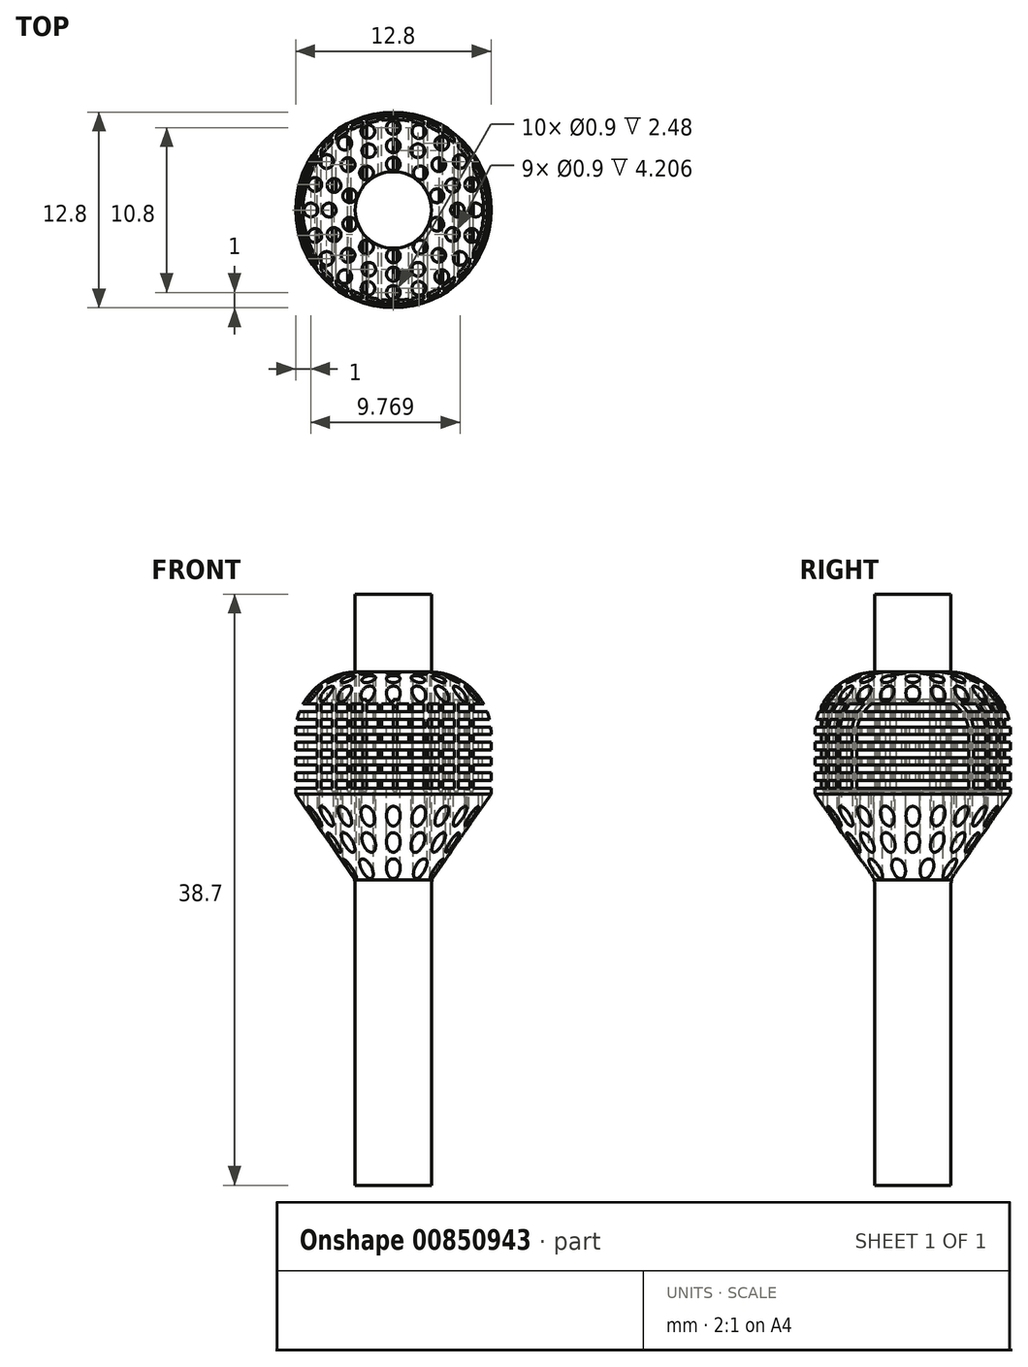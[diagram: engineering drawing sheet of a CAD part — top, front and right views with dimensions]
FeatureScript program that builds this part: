
annotation { "Feature Type Name" : "Feature", "Feature Type Description" : "" }
export const myFeature = defineFeature(function(context is Context, id is Id, definition is map)
    precondition{}
    {
        {
            var Q0;
            Q0=qCreatedBy(makeId("Front.planeOp"),FACE);
            var sketch = newSketch(context, id + "F0", { "sketchPlane" : qUnion([Q0])});
            skLineSegment(sketch, "E0", {"start": v(0, 0) * mm, "end": v(0, -20) * mm});
            skLineSegment(sketch, "E1", {"start": v(0, -20) * mm, "end": v(2.5, -20) * mm});
            skLineSegment(sketch, "E2", {"start": v(2.5, -20) * mm, "end": v(2.5, -0.32) * mm});
            skLineSegment(sketch, "E3", {"start": v(2.68, 0.26) * mm, "end": v(6.33, 5.48) * mm});
            skLineSegment(sketch, "E4", {"start": v(6.52, 6.05) * mm, "end": v(6.52, 9.73) * mm});
            skArc(sketch, "E5", {"start": v(6.52, 9.73) * mm, "mid": v(5.34, 12.57) * mm, "end": v(2.5, 13.73) * mm});
            skLineSegment(sketch, "E6", {"start": v(2.5, 13.73) * mm, "end": v(0, 13.72) * mm});
            skLineSegment(sketch, "E7", {"start": v(0, 0) * mm, "end": v(0, 13.72) * mm});
            skPoint(sketch, "E8.visualSharp", {"position": v(2.5, 0) * mm});
            skArc(sketch, "E8.filletArc", {"start": v(2.68, 0.26) * mm, "mid": v(2.55, -0.01) * mm, "end": v(2.5, -0.32) * mm});
            skPoint(sketch, "E9.visualSharp", {"position": v(6.52, 5.73) * mm});
            skArc(sketch, "E9.filletArc", {"start": v(6.33, 5.48) * mm, "mid": v(6.47, 5.75) * mm, "end": v(6.52, 6.05) * mm});
            skSolve(sketch);
        }
        {
            var Q0;
            Q0=makeQuery(id+"F0.imprint","IMPRINT",FACE,{"disambiguationData":[TD([[makeQuery(id+"F0.imprint","IMPRINT",EDGE,{"derivedFrom":sQuery(id+"F0.wireOp",EDGE,"E0")}),1.0]])]});
            var Q1;
            Q1=sQuery(id+"F0.wireOp",EDGE,"E7");
            revolve(context, id + "F1", {"surfaceOperationType" : NewSurfaceOperationType.NEW, "entities" : qUnion([Q0]), "axis" : qUnion([Q1]), "revolveType" : RevolveType.FULL});
        }
        {
            var Q0;
            Q0=qCreatedBy(makeId("Front.planeOp"),FACE);
            var sketch = newSketch(context, id + "F2", { "sketchPlane" : qUnion([Q0])});
            skLineSegment(sketch, "E10.bottom", {"start": v(2.5, 11.5) * mm, "end": v(7.5, 11.5) * mm});
            skLineSegment(sketch, "E10.top", {"start": v(2.5, 11) * mm, "end": v(7.5, 11) * mm});
            skLineSegment(sketch, "E10.left", {"start": v(2.5, 11.5) * mm, "end": v(2.5, 11) * mm});
            skLineSegment(sketch, "E10.right", {"start": v(7.5, 11.5) * mm, "end": v(7.5, 11) * mm});
            skLineSegment(sketch, "E11.0.1.0", {"start": v(2.5, 10) * mm, "end": v(7.5, 10) * mm});
            skLineSegment(sketch, "E11.0.1.1", {"start": v(2.5, 10.5) * mm, "end": v(7.5, 10.5) * mm});
            skLineSegment(sketch, "E11.0.1.2", {"start": v(2.5, 10.5) * mm, "end": v(2.5, 10) * mm});
            skLineSegment(sketch, "E11.0.1.3", {"start": v(7.5, 10.5) * mm, "end": v(7.5, 10) * mm});
            skLineSegment(sketch, "E11.0.2.0", {"start": v(2.5, 9) * mm, "end": v(7.5, 9) * mm});
            skLineSegment(sketch, "E11.0.2.1", {"start": v(2.5, 9.5) * mm, "end": v(7.5, 9.5) * mm});
            skLineSegment(sketch, "E11.0.2.2", {"start": v(2.5, 9.5) * mm, "end": v(2.5, 9) * mm});
            skLineSegment(sketch, "E11.0.2.3", {"start": v(7.5, 9.5) * mm, "end": v(7.5, 9) * mm});
            skLineSegment(sketch, "E11.0.3.0", {"start": v(2.5, 8) * mm, "end": v(7.5, 8) * mm});
            skLineSegment(sketch, "E11.0.3.1", {"start": v(2.5, 8.5) * mm, "end": v(7.5, 8.5) * mm});
            skLineSegment(sketch, "E11.0.3.2", {"start": v(2.5, 8.5) * mm, "end": v(2.5, 8) * mm});
            skLineSegment(sketch, "E11.0.3.3", {"start": v(7.5, 8.5) * mm, "end": v(7.5, 8) * mm});
            skLineSegment(sketch, "E11.direction1", {"start": v(2.5, 11) * mm, "end": v(27.5, 11) * mm, "construction": true});
            skLineSegment(sketch, "E11.direction2", {"start": v(2.5, 11) * mm, "end": v(2.5, 10) * mm, "construction": true});
            skLineSegment(sketch, "E12.0.0.4", {"start": v(2.5, 7) * mm, "end": v(7.5, 7) * mm});
            skLineSegment(sketch, "E12.3.0.4", {"start": v(2.5, 7.5) * mm, "end": v(7.5, 7.5) * mm});
            skLineSegment(sketch, "E12.6.0.4", {"start": v(2.5, 7.5) * mm, "end": v(2.5, 7) * mm});
            skLineSegment(sketch, "E12.9.0.4", {"start": v(7.5, 7.5) * mm, "end": v(7.5, 7) * mm});
            skLineSegment(sketch, "E13.0.0.5", {"start": v(2.5, 6) * mm, "end": v(7.5, 6) * mm});
            skLineSegment(sketch, "E13.3.0.5", {"start": v(2.5, 6.5) * mm, "end": v(7.5, 6.5) * mm});
            skLineSegment(sketch, "E13.6.0.5", {"start": v(2.5, 6.5) * mm, "end": v(2.5, 6) * mm});
            skLineSegment(sketch, "E13.9.0.5", {"start": v(7.5, 6.5) * mm, "end": v(7.5, 6) * mm});
            skSolve(sketch);
        }
        {
            var Q0;
            Q0=qCreatedBy(makeId("Front.planeOp"),FACE);
            var sketch = newSketch(context, id + "F3", { "sketchPlane" : qUnion([Q0])});
            skLineSegment(sketch, "E14", {"start": v(0, 35.11) * mm, "end": v(0, -39.83) * mm, "construction": true});
            skSolve(sketch);
        }
        {
            var Q0;
            Q0 = qSketchRegion(id + "F2", true);
            var Q1;
            Q1=sQuery(id+"F3.wireOp",EDGE,"E14");
            var Q2;
            Q2 = qConstructionFilter(qBodyType(qCreatedBy(id + "F2" ,EDGE), BodyType.WIRE), ConstructionObject.NO);
            var Q3;
            Q3=sQuery(id+"F3.wireOp",EDGE,"E14");
            revolve(context, id + "F4", {"operationType" : NewBodyOperationType.REMOVE, "surfaceOperationType" : NewSurfaceOperationType.NEW, "entities" : qUnion([Q0]), "surfaceEntities" : qUnion([Q1, Q2]), "axis" : qUnion([Q3]), "revolveType" : RevolveType.FULL, "oppositeDirection" : true});
        }
        {
            var Q0;
            Q0=qCreatedBy(makeId("Top.planeOp"),FACE);
            cPlane(context, id + "F5", {"entities" : qUnion([Q0]), "cplaneType" : CPlaneType.OFFSET, "offset" : 13.7 * mm, "width" : 150 * mm, "height" : 150 * mm});
        }
        {
            var Q0;
            Q0=qCreatedBy(id+"F5.planeOp",FACE);
            var sketch = newSketch(context, id + "F6", { "sketchPlane" : qUnion([Q0])});
            skCircle(sketch, "E15", {"center": v(0, 3) * mm, "radius": 0.45 * mm});
            skCircle(sketch, "E16.1.0", {"center": v(-1.76, 2.43) * mm, "radius": 0.45 * mm});
            skCircle(sketch, "E16.2.0", {"center": v(-2.85, 0.93) * mm, "radius": 0.45 * mm});
            skCircle(sketch, "E16.3.0", {"center": v(-2.85, -0.93) * mm, "radius": 0.45 * mm});
            skCircle(sketch, "E16.4.0", {"center": v(-1.76, -2.43) * mm, "radius": 0.45 * mm});
            skCircle(sketch, "E16.5.0", {"center": v(0, -3) * mm, "radius": 0.45 * mm});
            skCircle(sketch, "E16.6.0", {"center": v(1.76, -2.43) * mm, "radius": 0.45 * mm});
            skCircle(sketch, "E16.7.0", {"center": v(2.85, -0.93) * mm, "radius": 0.45 * mm});
            skCircle(sketch, "E16.8.0", {"center": v(2.85, 0.93) * mm, "radius": 0.45 * mm});
            skCircle(sketch, "E16.9.0", {"center": v(1.76, 2.43) * mm, "radius": 0.45 * mm});
            skPoint(sketch, "E16.center", {"position": v(0, 0) * mm});
            skCircle(sketch, "E17", {"center": v(0, 4.2) * mm, "radius": 0.45 * mm});
            skCircle(sketch, "E18.1.0", {"center": v(-1.6, 3.88) * mm, "radius": 0.45 * mm});
            skCircle(sketch, "E18.2.0", {"center": v(-2.97, 2.97) * mm, "radius": 0.45 * mm});
            skCircle(sketch, "E18.3.0", {"center": v(-3.88, 1.6) * mm, "radius": 0.45 * mm});
            skCircle(sketch, "E18.4.0", {"center": v(-4.2, 0) * mm, "radius": 0.45 * mm});
            skCircle(sketch, "E18.5.0", {"center": v(-3.88, -1.6) * mm, "radius": 0.45 * mm});
            skCircle(sketch, "E18.6.0", {"center": v(-2.97, -2.97) * mm, "radius": 0.45 * mm});
            skCircle(sketch, "E18.7.0", {"center": v(-1.6, -3.88) * mm, "radius": 0.45 * mm});
            skCircle(sketch, "E18.8.0", {"center": v(0, -4.2) * mm, "radius": 0.45 * mm});
            skCircle(sketch, "E18.9.0", {"center": v(1.6, -3.88) * mm, "radius": 0.45 * mm});
            skCircle(sketch, "E18.10.0", {"center": v(2.97, -2.97) * mm, "radius": 0.45 * mm});
            skCircle(sketch, "E18.11.0", {"center": v(3.88, -1.6) * mm, "radius": 0.45 * mm});
            skCircle(sketch, "E18.12.0", {"center": v(4.2, 0) * mm, "radius": 0.45 * mm});
            skCircle(sketch, "E18.13.0", {"center": v(3.88, 1.6) * mm, "radius": 0.45 * mm});
            skCircle(sketch, "E18.14.0", {"center": v(2.97, 2.97) * mm, "radius": 0.45 * mm});
            skCircle(sketch, "E18.15.0", {"center": v(1.6, 3.88) * mm, "radius": 0.45 * mm});
            skCircle(sketch, "E19", {"center": v(0, 5.4) * mm, "radius": 0.45 * mm});
            skCircle(sketch, "E20.1.0", {"center": v(-1.67, 5.14) * mm, "radius": 0.45 * mm});
            skCircle(sketch, "E20.2.0", {"center": v(-3.17, 4.37) * mm, "radius": 0.45 * mm});
            skCircle(sketch, "E20.3.0", {"center": v(-4.37, 3.17) * mm, "radius": 0.45 * mm});
            skCircle(sketch, "E20.4.0", {"center": v(-5.14, 1.67) * mm, "radius": 0.45 * mm});
            skCircle(sketch, "E20.5.0", {"center": v(-5.4, 0) * mm, "radius": 0.45 * mm});
            skCircle(sketch, "E20.6.0", {"center": v(-5.14, -1.67) * mm, "radius": 0.45 * mm});
            skCircle(sketch, "E20.7.0", {"center": v(-4.37, -3.17) * mm, "radius": 0.45 * mm});
            skCircle(sketch, "E20.8.0", {"center": v(-3.17, -4.37) * mm, "radius": 0.45 * mm});
            skCircle(sketch, "E20.9.0", {"center": v(-1.67, -5.14) * mm, "radius": 0.45 * mm});
            skCircle(sketch, "E20.10.0", {"center": v(0, -5.4) * mm, "radius": 0.45 * mm});
            skCircle(sketch, "E20.11.0", {"center": v(1.67, -5.14) * mm, "radius": 0.45 * mm});
            skCircle(sketch, "E20.12.0", {"center": v(3.17, -4.37) * mm, "radius": 0.45 * mm});
            skCircle(sketch, "E20.13.0", {"center": v(4.37, -3.17) * mm, "radius": 0.45 * mm});
            skCircle(sketch, "E20.14.0", {"center": v(5.14, -1.67) * mm, "radius": 0.45 * mm});
            skCircle(sketch, "E20.15.0", {"center": v(5.4, 0) * mm, "radius": 0.45 * mm});
            skCircle(sketch, "E20.16.0", {"center": v(5.14, 1.67) * mm, "radius": 0.45 * mm});
            skCircle(sketch, "E20.17.0", {"center": v(4.37, 3.17) * mm, "radius": 0.45 * mm});
            skCircle(sketch, "E20.18.0", {"center": v(3.17, 4.37) * mm, "radius": 0.45 * mm});
            skCircle(sketch, "E20.19.0", {"center": v(1.67, 5.14) * mm, "radius": 0.45 * mm});
            skSolve(sketch);
        }
        {
            var Q0;
            Q0 = qSketchRegion(id + "F6", true);
            extrude(context, id + "F7", {"entities" : qUnion([Q0]), "operationType" : NewBodyOperationType.REMOVE, "oppositeDirection" : true, "depth" : 16.5 * mm, "offsetDistance" : 25 * mm});
        }
        {
            var Q0;
            Q0=qCreatedBy(makeId("Front.planeOp"),FACE);
            cPlane(context, id + "F8", {"entities" : qUnion([Q0]), "cplaneType" : CPlaneType.OFFSET, "offset" : 6 * mm, "width" : 150 * mm, "height" : 150 * mm});
        }
        {
            var Q0;
            Q0=qCreatedBy(id+"F8.planeOp",FACE);
            var sketch = newSketch(context, id + "F9", { "sketchPlane" : qUnion([Q0])});
            skLineSegment(sketch, "E21.bottom", {"start": v(-4.75, 11.8) * mm, "end": v(-5, 11.8) * mm});
            skLineSegment(sketch, "E21.top", {"start": v(-4.75, 5.8) * mm, "end": v(-5, 5.8) * mm});
            skLineSegment(sketch, "E21.left", {"start": v(-4.75, 11.8) * mm, "end": v(-4.75, 5.8) * mm});
            skLineSegment(sketch, "E21.right", {"start": v(-5, 11.8) * mm, "end": v(-5, 5.8) * mm});
            skLineSegment(sketch, "E22.1.0.0", {"start": v(-4, 11.8) * mm, "end": v(-4, 5.8) * mm});
            skLineSegment(sketch, "E22.1.0.1", {"start": v(-3.75, 11.8) * mm, "end": v(-3.75, 5.8) * mm});
            skLineSegment(sketch, "E22.1.0.2", {"start": v(-3.75, 5.8) * mm, "end": v(-4, 5.8) * mm});
            skLineSegment(sketch, "E22.1.0.3", {"start": v(-3.75, 11.8) * mm, "end": v(-4, 11.8) * mm});
            skLineSegment(sketch, "E22.2.0.0", {"start": v(-3, 11.8) * mm, "end": v(-3, 5.8) * mm});
            skLineSegment(sketch, "E22.2.0.1", {"start": v(-2.75, 11.8) * mm, "end": v(-2.75, 5.8) * mm});
            skLineSegment(sketch, "E22.2.0.2", {"start": v(-2.75, 5.8) * mm, "end": v(-3, 5.8) * mm});
            skLineSegment(sketch, "E22.2.0.3", {"start": v(-2.75, 11.8) * mm, "end": v(-3, 11.8) * mm});
            skLineSegment(sketch, "E22.3.0.0", {"start": v(-2, 11.8) * mm, "end": v(-2, 5.8) * mm});
            skLineSegment(sketch, "E22.3.0.1", {"start": v(-1.75, 11.8) * mm, "end": v(-1.75, 5.8) * mm});
            skLineSegment(sketch, "E22.3.0.2", {"start": v(-1.75, 5.8) * mm, "end": v(-2, 5.8) * mm});
            skLineSegment(sketch, "E22.3.0.3", {"start": v(-1.75, 11.8) * mm, "end": v(-2, 11.8) * mm});
            skLineSegment(sketch, "E22.4.0.0", {"start": v(-1, 11.8) * mm, "end": v(-1, 5.8) * mm});
            skLineSegment(sketch, "E22.4.0.1", {"start": v(-0.75, 11.8) * mm, "end": v(-0.75, 5.8) * mm});
            skLineSegment(sketch, "E22.4.0.2", {"start": v(-0.75, 5.8) * mm, "end": v(-1, 5.8) * mm});
            skLineSegment(sketch, "E22.4.0.3", {"start": v(-0.75, 11.8) * mm, "end": v(-1, 11.8) * mm});
            skLineSegment(sketch, "E22.5.0.0", {"start": v(0, 11.8) * mm, "end": v(0, 5.8) * mm});
            skLineSegment(sketch, "E22.5.0.1", {"start": v(0.25, 11.8) * mm, "end": v(0.25, 5.8) * mm});
            skLineSegment(sketch, "E22.5.0.2", {"start": v(0.25, 5.8) * mm, "end": v(0, 5.8) * mm});
            skLineSegment(sketch, "E22.5.0.3", {"start": v(0.25, 11.8) * mm, "end": v(0, 11.8) * mm});
            skLineSegment(sketch, "E22.6.0.0", {"start": v(1, 11.8) * mm, "end": v(1, 5.8) * mm});
            skLineSegment(sketch, "E22.6.0.1", {"start": v(1.25, 11.8) * mm, "end": v(1.25, 5.8) * mm});
            skLineSegment(sketch, "E22.6.0.2", {"start": v(1.25, 5.8) * mm, "end": v(1, 5.8) * mm});
            skLineSegment(sketch, "E22.6.0.3", {"start": v(1.25, 11.8) * mm, "end": v(1, 11.8) * mm});
            skLineSegment(sketch, "E22.7.0.0", {"start": v(2, 11.8) * mm, "end": v(2, 5.8) * mm});
            skLineSegment(sketch, "E22.7.0.1", {"start": v(2.25, 11.8) * mm, "end": v(2.25, 5.8) * mm});
            skLineSegment(sketch, "E22.7.0.2", {"start": v(2.25, 5.8) * mm, "end": v(2, 5.8) * mm});
            skLineSegment(sketch, "E22.7.0.3", {"start": v(2.25, 11.8) * mm, "end": v(2, 11.8) * mm});
            skLineSegment(sketch, "E22.8.0.0", {"start": v(3, 11.8) * mm, "end": v(3, 5.8) * mm});
            skLineSegment(sketch, "E22.8.0.1", {"start": v(3.25, 11.8) * mm, "end": v(3.25, 5.8) * mm});
            skLineSegment(sketch, "E22.8.0.2", {"start": v(3.25, 5.8) * mm, "end": v(3, 5.8) * mm});
            skLineSegment(sketch, "E22.8.0.3", {"start": v(3.25, 11.8) * mm, "end": v(3, 11.8) * mm});
            skLineSegment(sketch, "E22.9.0.0", {"start": v(4, 11.8) * mm, "end": v(4, 5.8) * mm});
            skLineSegment(sketch, "E22.9.0.1", {"start": v(4.25, 11.8) * mm, "end": v(4.25, 5.8) * mm});
            skLineSegment(sketch, "E22.9.0.2", {"start": v(4.25, 5.8) * mm, "end": v(4, 5.8) * mm});
            skLineSegment(sketch, "E22.9.0.3", {"start": v(4.25, 11.8) * mm, "end": v(4, 11.8) * mm});
            skLineSegment(sketch, "E22.10.0.0", {"start": v(5, 11.8) * mm, "end": v(5, 5.8) * mm});
            skLineSegment(sketch, "E22.10.0.1", {"start": v(5.25, 11.8) * mm, "end": v(5.25, 5.8) * mm});
            skLineSegment(sketch, "E22.10.0.2", {"start": v(5.25, 5.8) * mm, "end": v(5, 5.8) * mm});
            skLineSegment(sketch, "E22.10.0.3", {"start": v(5.25, 11.8) * mm, "end": v(5, 11.8) * mm});
            skLineSegment(sketch, "E22.direction1", {"start": v(-5, 5.8) * mm, "end": v(-4, 5.8) * mm, "construction": true});
            skLineSegment(sketch, "E22.direction2", {"start": v(-5, 5.8) * mm, "end": v(-5, 3.8) * mm, "construction": true});
            skSolve(sketch);
        }
        {
            var Q0;
            Q0 = qSketchRegion(id + "F9", true);
            extrude(context, id + "F10", {"entities" : qUnion([Q0]), "operationType" : NewBodyOperationType.ADD, "oppositeDirection" : true, "depth" : 12 * mm, "offsetDistance" : 25 * mm});
        }
        {
            var Q0;
            Q0=qCreatedBy(makeId("Right.planeOp"),FACE);
            var sketch = newSketch(context, id + "F11", { "sketchPlane" : qUnion([Q0])});
            skLineSegment(sketch, "E23", {"start": v(-2.5, 0) * mm, "end": v(-6.4, 5.6) * mm});
            skLineSegment(sketch, "E24", {"start": v(-6.4, 5.6) * mm, "end": v(-6.4, 9.6) * mm});
            skArc(sketch, "E25", {"start": v(-2.4, 13.6) * mm, "mid": v(-5.23, 12.43) * mm, "end": v(-6.4, 9.6) * mm});
            skLineSegment(sketch, "E26", {"start": v(-2.4, 13.6) * mm, "end": v(-2.4, 16) * mm});
            skLineSegment(sketch, "E27", {"start": v(-2.4, 16) * mm, "end": v(-14.4, 16) * mm});
            skLineSegment(sketch, "E28", {"start": v(-14.4, 16) * mm, "end": v(-14.5, 0) * mm});
            skLineSegment(sketch, "E29", {"start": v(-14.5, 0) * mm, "end": v(-2.5, 0) * mm});
            skSolve(sketch);
        }
        {
            var Q0;
            Q0=qCreatedBy(makeId("Right.planeOp"),FACE);
            var sketch = newSketch(context, id + "F12", { "sketchPlane" : qUnion([Q0])});
            skLineSegment(sketch, "E30", {"start": v(0, -8.71) * mm, "end": v(0, 18.1) * mm, "construction": true});
            skSolve(sketch);
        }
        {
            var Q0;
            Q0=makeQuery(id+"F11.imprint","IMPRINT",FACE,{"disambiguationData":[TD([[makeQuery(id+"F11.imprint","IMPRINT",EDGE,{"derivedFrom":sQuery(id+"F11.wireOp",EDGE,"E23")}),1.0]])]});
            var Q1;
            Q1=sQuery(id+"F12.wireOp",EDGE,"E30");
            var Q2;
            Q2=sQuery(id+"F12.wireOp",EDGE,"E30");
            revolve(context, id + "F13", {"operationType" : NewBodyOperationType.REMOVE, "surfaceOperationType" : NewSurfaceOperationType.NEW, "entities" : qUnion([Q0]), "surfaceEntities" : qUnion([Q1]), "axis" : qUnion([Q2]), "revolveType" : RevolveType.FULL, "oppositeDirection" : true});
        }
        {
            var Q0;
            Q0=qCreatedBy(id+"F5.planeOp",FACE);
            var sketch = newSketch(context, id + "F14", { "sketchPlane" : qUnion([Q0])});
            skCircle(sketch, "E31", {"center": v(0, 0) * mm, "radius": 2.5 * mm});
            skSolve(sketch);
        }
        {
            var Q0;
            Q0 = qSketchRegion(id + "F14", true);
            extrude(context, id + "F15", {"entities" : qUnion([Q0]), "operationType" : NewBodyOperationType.ADD, "depth" : 5 * mm, "offsetDistance" : 25 * mm, "hasSecondDirection" : true, "secondDirectionOppositeDirection" : true, "secondDirectionDepth" : 1 * mm});
        }
    });
